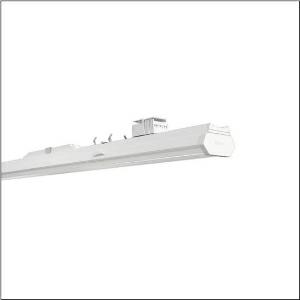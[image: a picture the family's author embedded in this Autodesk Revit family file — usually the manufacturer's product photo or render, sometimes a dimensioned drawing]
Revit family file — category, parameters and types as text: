
# Revit family: licross_21_protected_ho_52tp12dn4e5m
name_source: partatom
category: Lighting Fixtures
units: mm (PartAtom-declared; Revit-internal decimal feet)

## family parameters
Cut with Voids When Loaded = No
Host = Face
Light Source = No
Part Type = Normal
Room Calculation Point = No
Round Connector Dimension = Use Diameter
Shared = No

## types (1)
- --- (1 x LED, 14690 lm, 84.9 W, 4000K)
    Apparent Load = 85 VA
    CIE Flux Codes = 70 91 97 98 100
    Color Rendering = 80
    Color Temperature = 4000K
    Default Elevation = 1800 mm
    Description = Licross 21 Protected HO, luminaire insert, of sheet steel, galvanised, coil coated, white, length: 1.500mm, width: 90mm, height: 103mm, LED rated luminous flux: 14.690lm, light colour: 840, SDCM (Standard Deviation of Colour Matching)MacAdam ≤ 3 SDCM (initial), control gear: DALI 2, with plug, 5-pole, with phase selection, mains connection: 220..240V, AC, 50/60Hz, rated input power: 85W, internal wiring halogen-free, primary light control with lens, of plastic, primary optical cover: cover, of PMMA, light emission: direct distribution, primary light characteristic: symmetric, protection rating (complete): IP64, insulation class (complete): insulation class I (protective earthing), certification: CE, ENEC, VDE, UKCA, protection symbol: D if used in an environment with conductive dust loads with corresponding accessories, impact resistance: IK06, permissible ambient temperature for indoor applications: -25..+35°C, corresponds to IFS (International Featured Standards) requirements for safety and quality in the food industry, reducing of maximum allowable ambient temperature of 5°C with ceiling mounting, LABS conformity tested according to VDMA 24364:2018-05, The light source and the operating device comply with the requirements of the Ecodesign Regulation (EU) 2019/2020 and are replaceable in accordance with this regulation, packaging unit: 1 piece
    Height = 92 mm
    Lamp = 1 x LED
    Lamp Light Flux = 14690 lm
    Lamp Power = 84.9 W
    Lamp count = 1
    Length = 1500 mm
    Luminous efficacy = 173 lm/W
    Manufacturer = Siteco
    ModVariant = No
    Model = 52TP12DN4E5M
    Mounting Place = Ceiling
    Mounting Type = Pendant
    Number of Poles = 1
    OnlyDefault = Yes
    Power Factor = 1
    Product Name = Licross 21 Protected HO
    Product group = luminaire insert | ceiling pendant
    ProductGroupID = 901
    Protection Class = Protection class I
    Protection Degree = IP 64
    RLX_Detail_Level = 1
    RLX_Emergency_Light_Flux = 0 lm
    RLX_Emergency_Type = 0
    RLX_Emergency_Type_DB = No
    RlxData = <blob elided: 24761 chars, md5=5a304c5b>
    Socket = socket
    Standby Power = 0 W
    System Light Flux = 14690 lm
    System Power = 85 W
    Type Comments = factory setting: luminous flux: 100 % | dim-lin: 254 | 484 mA
    Type Image = l_1256148.jpg
    URL = http://relux.com
    VarID = @adj_129053
    Voltage = 0 V
    Weight = 0.00 kg
    Width = 88 mm

## geometry (parser evidence)
native form markers: Blend x4, Sweep x11
no freeform markers — native parametric forms only
